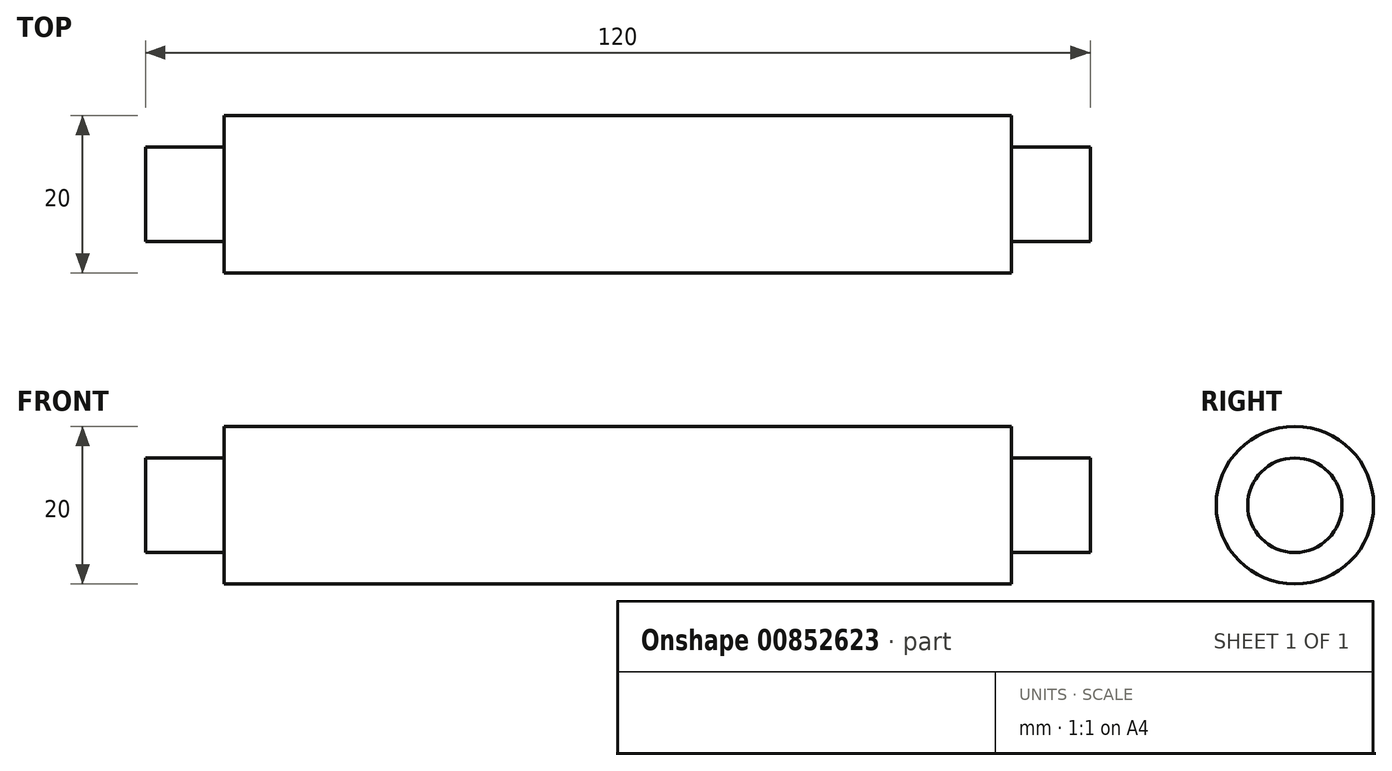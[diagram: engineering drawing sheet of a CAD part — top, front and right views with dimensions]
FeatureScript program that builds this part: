
annotation { "Feature Type Name" : "Feature", "Feature Type Description" : "" }
export const myFeature = defineFeature(function(context is Context, id is Id, definition is map)
    precondition{}
    {
        {
            var Q0;
            Q0=qCreatedBy(makeId("Top.planeOp"),FACE);
            var sketch = newSketch(context, id + "F0", { "sketchPlane" : qUnion([Q0])});
            skLineSegment(sketch, "E0", {"start": v(0, 0) * mm, "end": v(0, 6) * mm});
            skLineSegment(sketch, "E1", {"start": v(0, 6) * mm, "end": v(10, 6) * mm});
            skLineSegment(sketch, "E2", {"start": v(10, 6) * mm, "end": v(10, 10) * mm});
            skLineSegment(sketch, "E3", {"start": v(10, 10) * mm, "end": v(110, 10) * mm});
            skLineSegment(sketch, "E4", {"start": v(110, 10) * mm, "end": v(110, 6) * mm});
            skLineSegment(sketch, "E5", {"start": v(110, 6) * mm, "end": v(120, 6) * mm});
            skLineSegment(sketch, "E6", {"start": v(120, 6) * mm, "end": v(120, 0) * mm});
            skLineSegment(sketch, "E7", {"start": v(120, 0) * mm, "end": v(0, 0) * mm});
            skSolve(sketch);
        }
        {
            var Q0;
            Q0=makeQuery(id+"F0.imprint","IMPRINT",FACE,{"disambiguationData":[TD([[makeQuery(id+"F0.imprint","IMPRINT",EDGE,{"derivedFrom":sQuery(id+"F0.wireOp",EDGE,"E0")}),-1.0]])]});
            var Q1;
            Q1=sQuery(id+"F0.wireOp",EDGE,"E7");
            revolve(context, id + "F1", {"surfaceOperationType" : NewSurfaceOperationType.NEW, "entities" : qUnion([Q0]), "axis" : qUnion([Q1]), "revolveType" : RevolveType.FULL});
        }
    });
